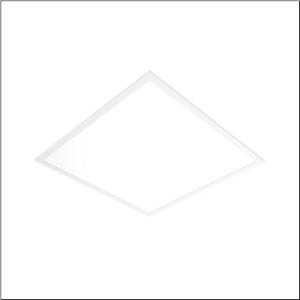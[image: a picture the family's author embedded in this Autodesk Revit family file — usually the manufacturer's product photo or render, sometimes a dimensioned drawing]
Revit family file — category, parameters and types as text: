
# Revit family: apollon_r__41_51mh12w72343_d43e
name_source: partatom
category: Lighting Fixtures
units: mm (PartAtom-declared; Revit-internal decimal feet)

## family parameters
Cut with Voids When Loaded = No
Host = Face
Light Source = No
Part Type = Normal
Room Calculation Point = No
Round Connector Dimension = Use Diameter
Shared = No

## types (1)
- Apollon® 41 (1 x LED, 3500 lm, 28.5 W, 3000K)
    Apparent Load = 29 VA
    CIE Flux Codes = 61 87 97 100 100
    Color Rendering = 80
    Color Temperature = 3000K
    Default Elevation = 1800 mm
    Description = Apollon® 41, office luminaire, primary optical cover: prismatic diffuser, of PS, light emission: direct distribution, primary light characteristic: symmetric, installation type: lay-in mounting, LED, rated luminous flux: 3.500lm, luminous efficacy: 123lm/W, light colour: 830, colour temperature: 3000K, with terminal, 3-pole, mains connection: 220..240V, AC, 50/60Hz, housing, of aluminium section, traffic white (RAL 9016), module: M600, length: 600mm, width: 600mm, height: 28mm, housing upper side, of sheet steel, protection rating (complete): IP20, protection rating (lamp compartment, on room side): IP40, insulation class (complete): insulation class II (safety insulation), certification: CE, ENEC, permissible operating ambient temperature: -25..+40°C, packaging unit: 1 piece
    Height = 0 mm  [stored 0 ft]
    Lamp = 1 x LED
    Lamp Light Flux = 3500 lm
    Lamp Power = 28.5 W
    Lamp count = 1
    Length = 600 mm
    Luminous efficacy = 123 lm/W
    Manufacturer = Siteco
    ModVariant = No
    Model = 51MH12W72343
    Mounting Place = Ceiling
    Mounting Type = Recessed
    Number of Poles = 1
    OnlyDefault = Yes
    Power Factor = 1
    Product Name = Apollon® 41
    Product group = office luminaire | ceiling recessed
    ProductGroupID = 400
    Protection Class = Protection class II
    Protection Degree = IP 20
    RLX_Detail_Level = 1
    RLX_Emergency_Light_Flux = 0 lm
    RLX_Emergency_Type = 0
    RLX_Emergency_Type_DB = No
    RlxData = <blob elided: 12181 chars, md5=178b07f7>
    Socket = socket
    Standby Power = 0 W
    System Light Flux = 3500 lm
    System Power = 29 W
    Type Comments = Product without accessories
    Type Image = l_1291024.jpg
    URL = http://relux.com
    VarID = ---
    Voltage = 0 V
    Weight = 0.00 kg
    Width = 600 mm

note: [stored X ft] marks values corroborated as IEEE doubles in the binary element streams (Revit-internal decimal feet)

## geometry (parser evidence)
native form markers: Sweep x8
no freeform markers — native parametric forms only
